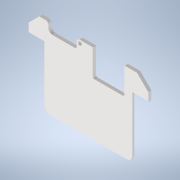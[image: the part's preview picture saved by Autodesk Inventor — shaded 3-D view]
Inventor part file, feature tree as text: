
AUTODESK INVENTOR PART (.ipt)
format: ipt  version: 2020 (Build 240168000, 168)  size: 224,768 bytes
history: native  units: mm
features: extrude x4, sketch x4, projected_geometry x3, chamfer x2, plane x1, direct_edit x1, move_body x1
ambient origin geometry x8: Origin, YZ Plane, XZ Plane, XY Plane, X Axis, Y Axis, Z Axis, Center Point
bodies: Solid1 (feature_tree)
feature tree (16):
  extrude  "Extrusion1"  Depth=168.0mm
  extrude  "Extrusion2"  Depth=10.0mm TaperAngle=0.0deg
  chamfer  "Chamfer2"  Distance=85.0mm
  chamfer  "Chamfer3"  Distance=75.0mm
  extrude  "Extrusion3"  TaperAngle=135.0deg  [1 undecoded]
  plane  "Work Plane1"
  extrude  "Extrusion4"  Depth=10.0mm
  direct_edit  "Direct Edit1"
  sketch  "Sketch1"  dims[d0=278.0mm d1=168.0mm]
  sketch  "Sketch2"  dims[d2=19.0mm d3=10.0mm d4=0.0mm]
  projected_geometry  "Projected Loop1"
  sketch  "Sketch3"  dims[d8=21.0mm]
  projected_geometry  "Projected Loop2"
  projected_geometry  "Projected Loop3"
  sketch  "Sketch4"  dims[d9=50.0mm d10=85.0mm d11=75.0mm d12=135.0deg d13=40.0mm d14=100.0mm d16=90.0mm d17=50.0mm d19=34.0mm d20=135.0deg d21=5.0mm d22=1.0mm d23=14.0mm d24=5.0mm d26=90.0mm d29=12.0mm d30=226.0mm d31=5.0mm d32=5.0mm d33=55.0mm d34=20.0mm d35=16.0mm d36=75.0mm d37=112.0mm d38=26.0mm d39=10.0mm d40=0.0mm d41=4.0mm d42=2.0mm d43=45.0deg d44=4.0mm d45=2.0mm d46=45.0deg d47=45.0deg d48=4.0mm d49=10.0mm d50=0.0mm d51=10.0mm d52=0.0mm d53=0.0mm d54=0.0mm d55=-1.0mm]
  move_body  "Move1"
note: 1 required parameter value undecoded (feature->parameter linkage not recoverable at this tier; creation-order binding heuristic only, values carry confidence <= 0.55)
